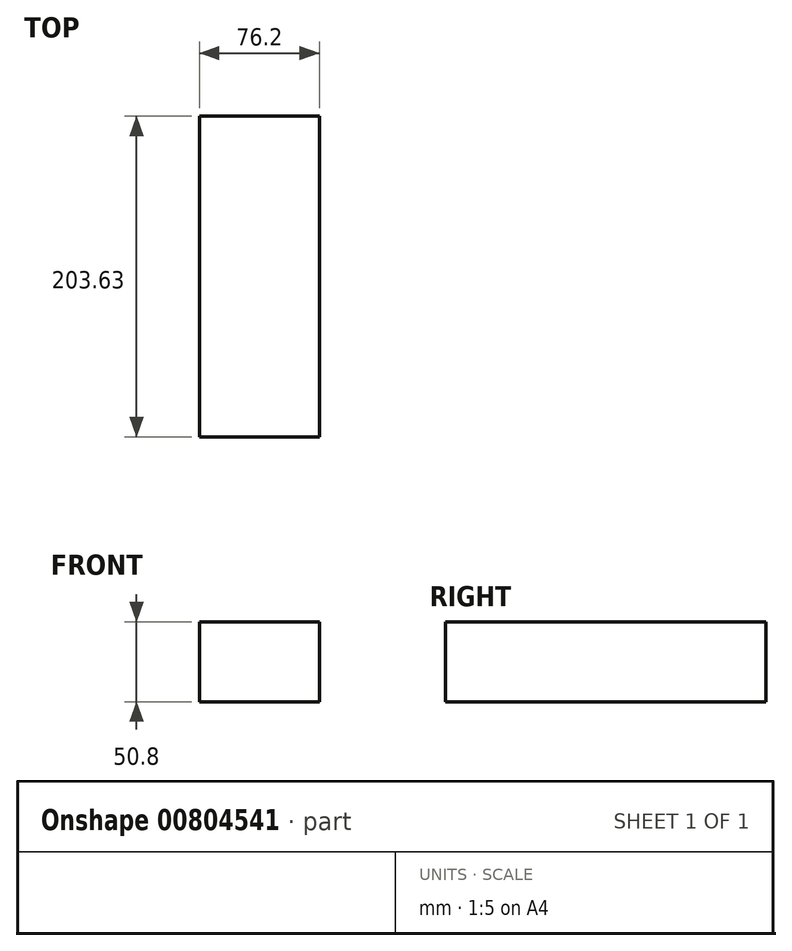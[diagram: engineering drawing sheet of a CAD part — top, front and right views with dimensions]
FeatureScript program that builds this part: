
annotation { "Feature Type Name" : "Feature", "Feature Type Description" : "" }
export const myFeature = defineFeature(function(context is Context, id is Id, definition is map)
    precondition{}
    {
        {
            var Q0;
            Q0=qCreatedBy(makeId("Top.planeOp"),FACE);
            var sketch = newSketch(context, id + "F0", { "sketchPlane" : qUnion([Q0])});
            skLineSegment(sketch, "E0.bottom", {"start": v(-32.75, 47.63) * mm, "end": v(43.45, 47.63) * mm});
            skLineSegment(sketch, "E0.top", {"start": v(-32.75, -156) * mm, "end": v(43.45, -156) * mm});
            skLineSegment(sketch, "E0.left", {"start": v(-32.75, 47.63) * mm, "end": v(-32.75, -156) * mm});
            skLineSegment(sketch, "E0.right", {"start": v(43.45, 47.63) * mm, "end": v(43.45, -156) * mm});
            skSolve(sketch);
        }
        {
            var Q0;
            Q0=makeQuery(id+"F0.imprint","IMPRINT",FACE,{"disambiguationData":[TD([[makeQuery(id+"F0.imprint","IMPRINT",EDGE,{"derivedFrom":sQuery(id+"F0.wireOp",EDGE,"E0.bottom")}),-1.0]])]});
            extrude(context, id + "F1", {"entities" : qUnion([Q0]), "depth" : 50.8 * mm, "offsetDistance" : 25.4 * mm});
        }
    });
